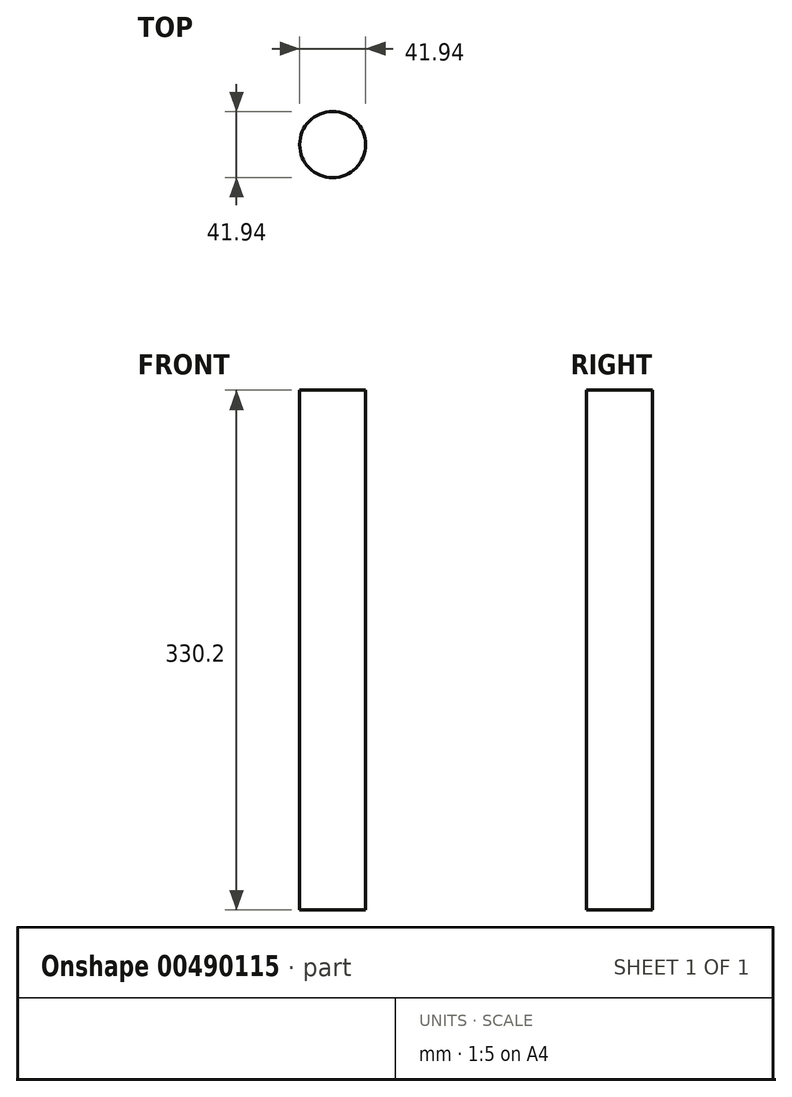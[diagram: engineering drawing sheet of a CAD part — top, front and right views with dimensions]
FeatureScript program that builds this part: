
annotation { "Feature Type Name" : "Feature", "Feature Type Description" : "" }
export const myFeature = defineFeature(function(context is Context, id is Id, definition is map)
    precondition{}
    {
        {
            var Q0;
            Q0=qCreatedBy(makeId("Top.planeOp"),FACE);
            var sketch = newSketch(context, id + "F0", { "sketchPlane" : qUnion([Q0])});
            skCircle(sketch, "E0", {"center": v(44.5, -45.03) * mm, "radius": 20.97 * mm});
            skSolve(sketch);
        }
        {
            var Q0;
            Q0=makeQuery(id+"F0.imprint","IMPRINT",FACE,{"disambiguationData":[TD([[makeQuery(id+"F0.imprint","IMPRINT",EDGE,{"derivedFrom":sQuery(id+"F0.wireOp",EDGE,"E0")}),1.0]])]});
            extrude(context, id + "F1", {"entities" : qUnion([Q0]), "depth" : 330.2 * mm});
        }
    });
